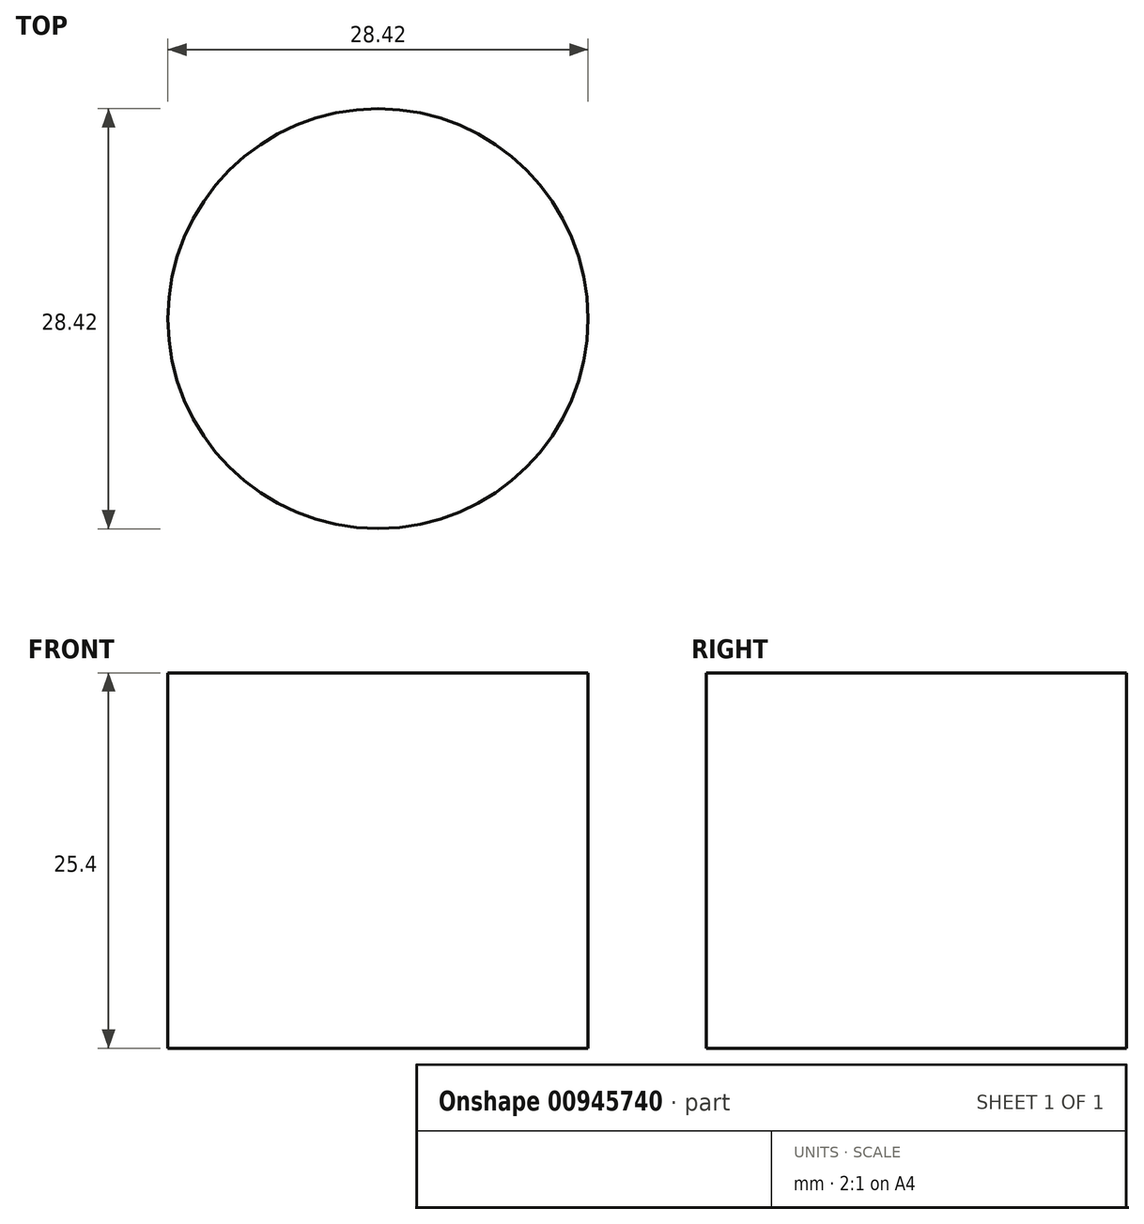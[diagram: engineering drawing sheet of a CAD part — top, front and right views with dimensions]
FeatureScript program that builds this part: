
annotation { "Feature Type Name" : "Feature", "Feature Type Description" : "" }
export const myFeature = defineFeature(function(context is Context, id is Id, definition is map)
    precondition{}
    {
        {
            var Q0;
            Q0=qCreatedBy(makeId("Top.planeOp"),FACE);
            var sketch = newSketch(context, id + "F0", { "sketchPlane" : qUnion([Q0])});
            skCircle(sketch, "E0", {"center": v(-23.6, 20.62) * mm, "radius": 14.21 * mm});
            skSolve(sketch);
        }
        {
            var Q0;
            Q0 = qSketchRegion(id + "F0", true);
            extrude(context, id + "F1", {"entities" : qUnion([Q0]), "depth" : 25.4 * mm, "offsetDistance" : 25.4 * mm});
        }
    });
